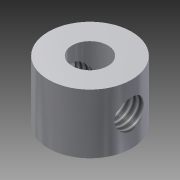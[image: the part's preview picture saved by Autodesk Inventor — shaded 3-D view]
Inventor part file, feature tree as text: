
AUTODESK INVENTOR PART (.ipt)
format: ipt  version: 2015 (Build 190159000, 159)  size: 145,408 bytes
history: native  units: mm
features: sketch x4, extrude x2, hole x2, other x1
ambient origin geometry x8: Origin, YZ Plane, XZ Plane, XY Plane, X Axis, Y Axis, Z Axis, Center Point
bodies: Body1 (feature_tree)
feature tree (9):
  other  "ソリッド1"
  extrude  "押し出し1"  Depth=7.0mm
  hole  "穴1"  [1 undecoded]
  extrude  "押し出し2"  Depth=5.0mm TaperAngle=0.0deg
  hole  "穴2"  [1 undecoded]
  sketch  "スケッチ1"
  sketch  "スケッチ2"
  sketch  "スケッチ3"
  sketch  "スケッチ4"
note: 2 required parameter values undecoded (feature->parameter linkage not recoverable at this tier; creation-order binding heuristic only, values carry confidence <= 0.55)
